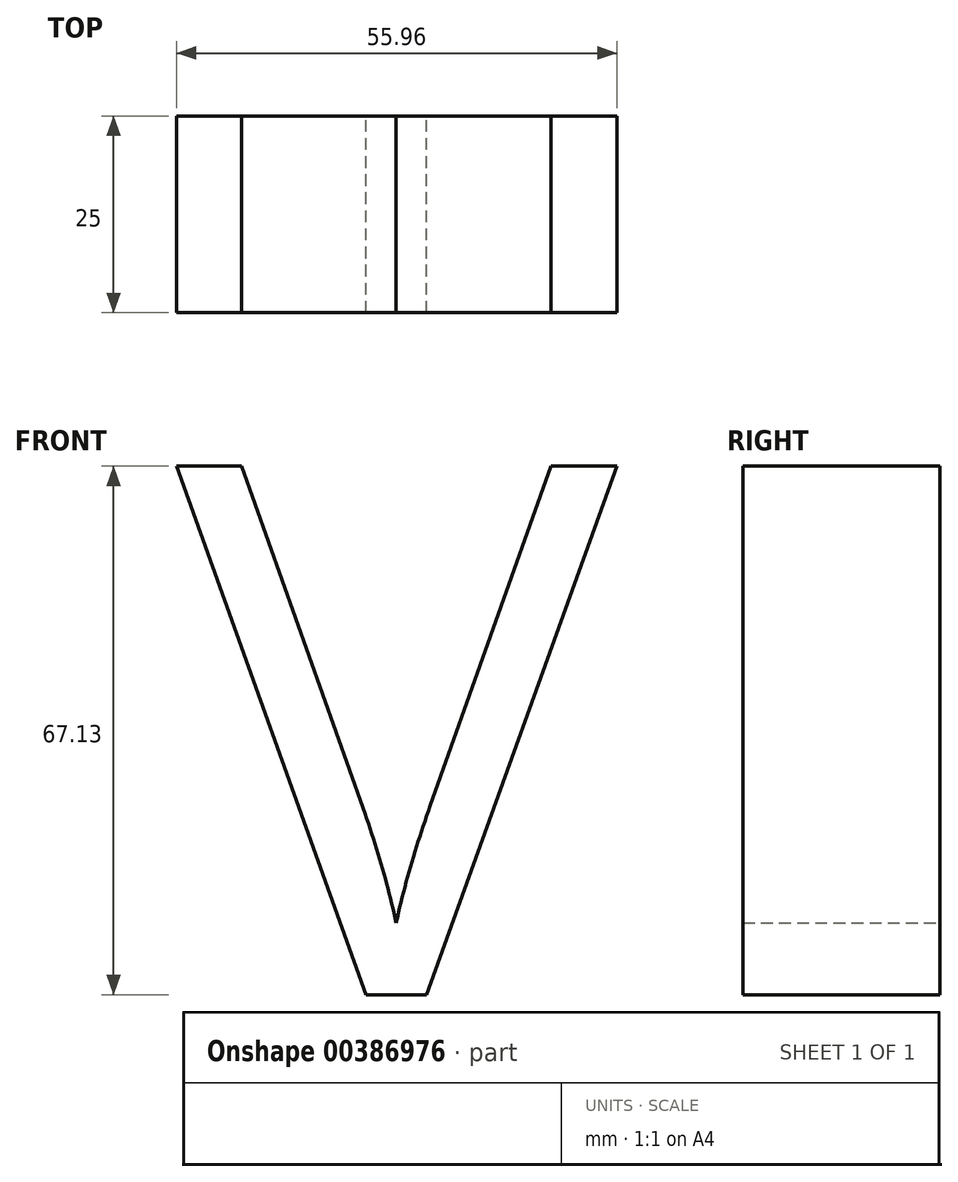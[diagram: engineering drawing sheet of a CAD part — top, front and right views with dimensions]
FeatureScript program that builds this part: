
annotation { "Feature Type Name" : "Feature", "Feature Type Description" : "" }
export const myFeature = defineFeature(function(context is Context, id is Id, definition is map)
    precondition{}
    {
        {
            var Q0;
            Q0=qCreatedBy(makeId("Front.planeOp"),FACE);
            var sketch = newSketch(context, id + "F0", { "sketchPlane" : qUnion([Q0])});
            skText(sketch, "E0", { "text": "V", "fontName": "OpenSans-Regular.ttf"});
            const initialGuessF0  = {"E0": [-0.04941, -0.03184, 1, 0, 0.0677]};
            skSetInitialGuess(sketch, initialGuessF0);
            skSolve(sketch);
        }
        {
            var Q0;
            Q0 = qSketchRegion(id + "F0", true);
            extrude(context, id + "F1", {"entities" : qUnion([Q0]), "depth" : 25 * mm});
        }
    });
